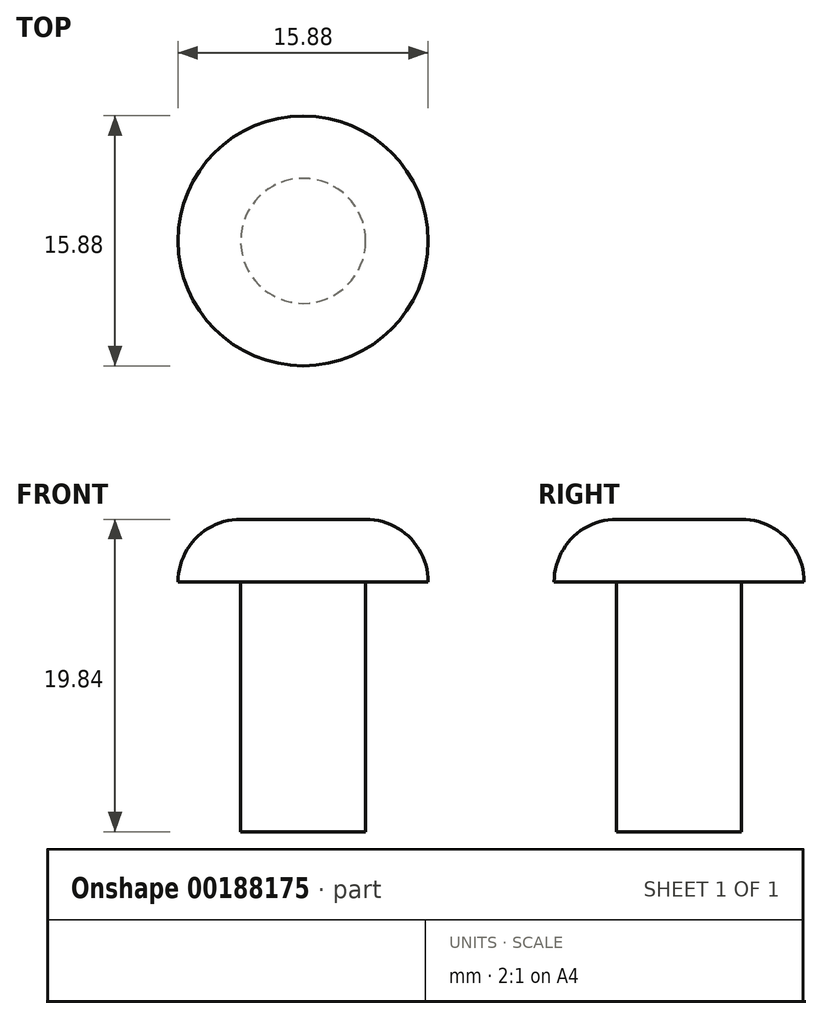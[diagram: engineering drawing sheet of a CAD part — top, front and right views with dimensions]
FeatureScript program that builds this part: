
annotation { "Feature Type Name" : "Feature", "Feature Type Description" : "" }
export const myFeature = defineFeature(function(context is Context, id is Id, definition is map)
    precondition{}
    {
        {
            var Q0;
            Q0=qCreatedBy(makeId("Front.planeOp"),FACE);
            var sketch = newSketch(context, id + "F0", { "sketchPlane" : qUnion([Q0])});
            skLineSegment(sketch, "E0", {"start": v(0, 0) * mm, "end": v(3.97, 0) * mm});
            skLineSegment(sketch, "E1", {"start": v(3.97, 0) * mm, "end": v(3.97, 15.88) * mm});
            skLineSegment(sketch, "E2", {"start": v(3.97, 15.88) * mm, "end": v(7.94, 15.88) * mm});
            skLineSegment(sketch, "E3", {"start": v(0, 0) * mm, "end": v(0, 19.84) * mm});
            skLineSegment(sketch, "E4", {"start": v(0, 19.84) * mm, "end": v(3.97, 19.84) * mm});
            skLineSegment(sketch, "E5", {"start": v(0, 23.19) * mm, "end": v(0, -15.19) * mm, "construction": true});
            skArc(sketch, "E6", {"start": v(7.94, 15.88) * mm, "mid": v(6.78, 18.68) * mm, "end": v(3.97, 19.84) * mm});
            skSolve(sketch);
        }
        {
            var Q0;
            Q0=makeQuery(id+"F0.imprint","IMPRINT",FACE,{"disambiguationData":[TD([[makeQuery(id+"F0.imprint","IMPRINT",EDGE,{"derivedFrom":sQuery(id+"F0.wireOp",EDGE,"E0")}),1.0]])]});
            var Q1;
            Q1=sQuery(id+"F0.wireOp",EDGE,"E5");
            revolve(context, id + "F1", {"entities" : qUnion([Q0]), "axis" : qUnion([Q1]), "revolveType" : RevolveType.FULL});
        }
    });
